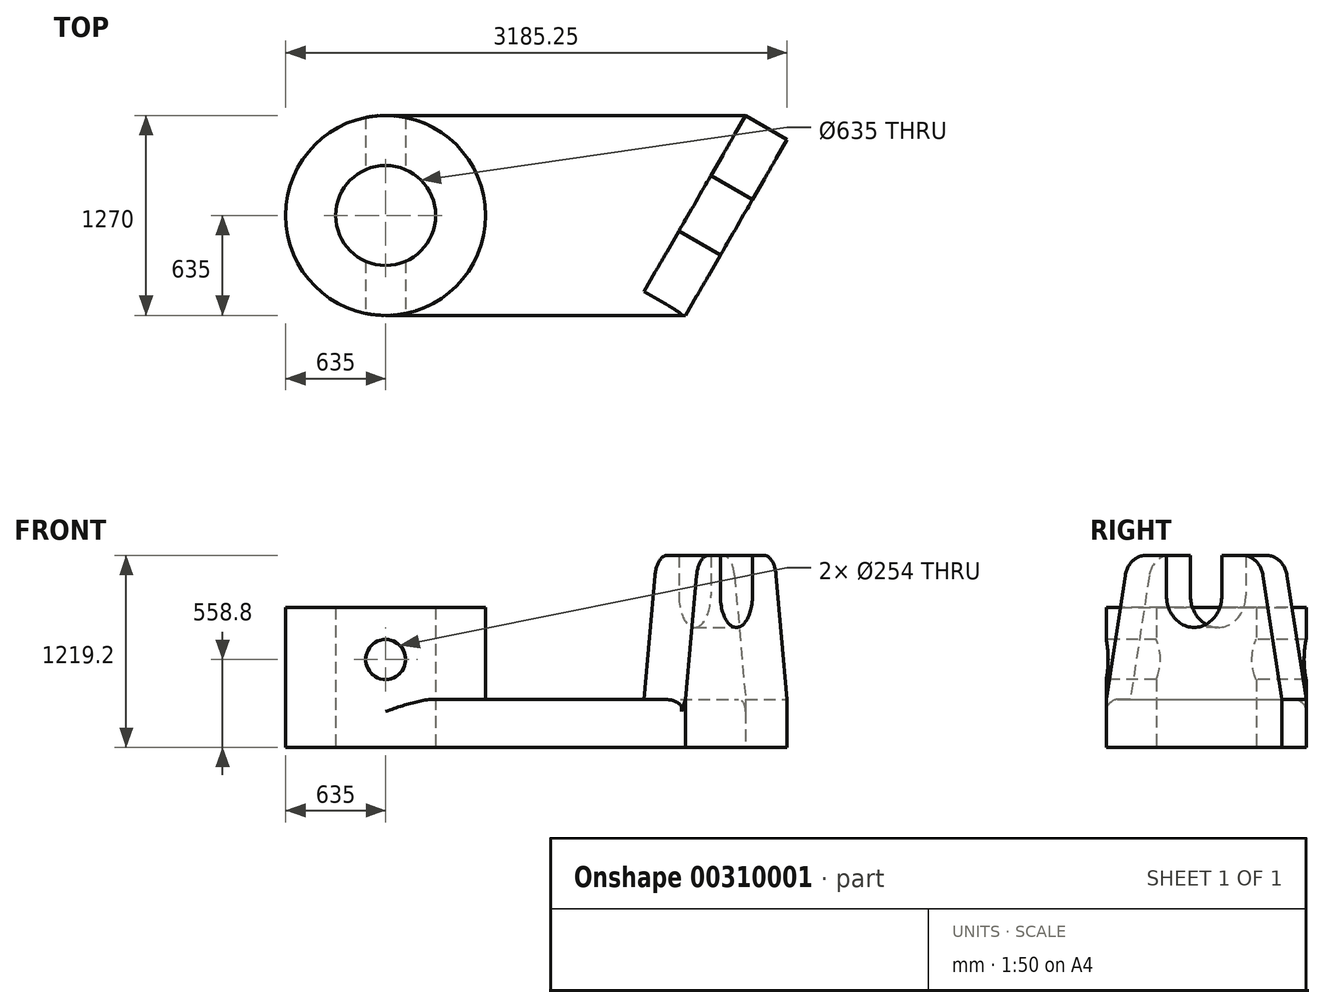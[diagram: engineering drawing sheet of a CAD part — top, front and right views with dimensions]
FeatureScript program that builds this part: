
annotation { "Feature Type Name" : "Feature", "Feature Type Description" : "" }
export const myFeature = defineFeature(function(context is Context, id is Id, definition is map)
    precondition{}
    {
        {
            var Q0;
            Q0=qCreatedBy(makeId("Top.planeOp"),FACE);
            var sketch = newSketch(context, id + "F0", { "sketchPlane" : qUnion([Q0])});
            skCircle(sketch, "E0", {"center": v(0, 0) * mm, "radius": 635 * mm});
            skCircle(sketch, "E1", {"center": v(0, 0) * mm, "radius": 317.5 * mm});
            skLineSegment(sketch, "E2.top", {"start": v(0, -635) * mm, "end": v(1905, -635) * mm});
            skLineSegment(sketch, "E3", {"start": v(1905, -635) * mm, "end": v(1641.04, -482.6) * mm});
            skLineSegment(sketch, "E4", {"start": v(1641.04, -482.6) * mm, "end": v(2286.28, 635) * mm});
            skLineSegment(sketch, "E5", {"start": v(1905, -635) * mm, "end": v(2550.25, 482.6) * mm});
            skLineSegment(sketch, "E6", {"start": v(2286.28, 635) * mm, "end": v(2550.25, 482.6) * mm});
            skLineSegment(sketch, "E7", {"start": v(0, 635) * mm, "end": v(2286.28, 635) * mm});
            skSolve(sketch);
        }
        {
            var Q0;
            Q0=makeQuery(id+"F0.imprint","IMPRINT",FACE,{"disambiguationData":[TD([[makeQuery(id+"F0.imprint","IMPRINT",EDGE,{"derivedFrom":sQuery(id+"F0.wireOp",EDGE,"E1")}),-1.0]])]});
            extrude(context, id + "F1", {"entities" : qUnion([Q0]), "depth" : 889 * mm});
        }
        {
            var Q0;
            {var subQ0=sQuery(id+"F0.wireOp",EDGE,"E2.top");Q0=makeQuery(id+"F0.imprint","IMPRINT",FACE,{"disambiguationData":[TD([[makeQuery(id+"F0.imprint","IMPRINT",EDGE,{"derivedFrom":subQ0}),1.0]])]});}
            var Q1;
            Q1=makeQuery(id+"F0.imprint","IMPRINT",FACE,{"disambiguationData":[TD([[makeQuery(id+"F0.imprint","IMPRINT",EDGE,{"derivedFrom":sQuery(id+"F0.wireOp",EDGE,"E3")}),-1.0]])]});
            extrude(context, id + "F2", {"entities" : qUnion([Q0, Q1]), "operationType" : NewBodyOperationType.ADD, "depth" : 304.8 * mm});
        }
        {
            var Q0;
            Q0=makeQuery(id+"F2.opExtrude","SWEPT_FACE",FACE,{"disambiguationData":[OSD([sQuery(id+"F0.wireOp",EDGE,"E5")])]});
            var sketch = newSketch(context, id + "F3", { "sketchPlane" : qUnion([Q0])});
            skLineSegment(sketch, "E8", {"start": v(692.9, 1219.2) * mm, "end": v(844.62, 1219.2) * mm});
            skLineSegment(sketch, "E9", {"start": v(1251.02, 1219.2) * mm, "end": v(1402.74, 1219.2) * mm});
            skLineSegment(sketch, "E10", {"start": v(1552.78, 1093.49) * mm, "end": v(1693.07, 304.8) * mm});
            skLineSegment(sketch, "E11", {"start": v(542.86, 1093.49) * mm, "end": v(402.57, 304.8) * mm});
            skPoint(sketch, "E12.visualSharp", {"position": v(1530.42, 1219.2) * mm});
            skArc(sketch, "E12.filletArc", {"start": v(1552.78, 1093.49) * mm, "mid": v(1500.6, 1183.62) * mm, "end": v(1402.74, 1219.2) * mm});
            skPoint(sketch, "E13.visualSharp", {"position": v(565.22, 1219.2) * mm});
            skArc(sketch, "E13.filletArc", {"start": v(692.9, 1219.2) * mm, "mid": v(595.03, 1183.62) * mm, "end": v(542.86, 1093.49) * mm});
            skLineSegment(sketch, "E14", {"start": v(692.9, 1219.2) * mm, "end": v(542.86, 1219.2) * mm, "construction": true});
            skLineSegment(sketch, "E15", {"start": v(1402.74, 1219.2) * mm, "end": v(1552.78, 1219.2) * mm, "construction": true});
            skLineSegment(sketch, "E16", {"start": v(844.62, 1219.2) * mm, "end": v(844.62, 965.2) * mm});
            skLineSegment(sketch, "E17", {"start": v(1251.02, 1219.2) * mm, "end": v(1251.02, 965.2) * mm});
            skPoint(sketch, "E18.centerSnap0", {"position": v(1047.82, 304.8) * mm});
            skArc(sketch, "E19", {"start": v(844.62, 965.2) * mm, "mid": v(1047.82, 762) * mm, "end": v(1251.02, 965.2) * mm});
            skSolve(sketch);
        }
        {
            var Q0;
            Q0=makeQuery(id+"F3.imprint","IMPRINT",FACE,{"disambiguationData":[TD([[makeQuery(id+"F3.imprint","IMPRINT",EDGE,{"derivedFrom":sQuery(id+"F3.wireOp",EDGE,"E8")}),-1.0]])]});
            extrude(context, id + "F4", {"entities" : qUnion([Q0]), "operationType" : NewBodyOperationType.ADD, "oppositeDirection" : true, "depth" : 304.8 * mm});
        }
        {
            var Q0;
            Q0=makeQuery(id+"F2.opExtrude","SWEPT_FACE",FACE,{"disambiguationData":[OSD([sQuery(id+"F0.wireOp",EDGE,"E2.top")])]});
            var sketch = newSketch(context, id + "F5", { "sketchPlane" : qUnion([Q0])});
            skPoint(sketch, "E20", {"position": v(0, 558.8) * mm});
            skSolve(sketch);
        }
        {
            var Q0;
            Q0=sQuery(id+"F5.wireOp",VERTEX,"E20");
            var Q1;
            Q1=makeQuery(id+"F1.opExtrude","SWEPT_BODY",BODY,{"disambiguationData":[OSD([sQuery(id+"F0.wireOp",EDGE,"E0"),sQuery(id+"F0.wireOp",EDGE,"E1")])]});
            hole(context, id + "F6", {"style" : HoleStyle.SIMPLE, "endStyle" : HoleEndStyle.THROUGH, "holeDiameter" : 254 * mm, "tappedDepth" : 12.7 * mm, "tapClearance" : 3, "locations" : qUnion([Q0]), "scope" : qUnion([Q1])});
        }
        {
            var Q0;
            Q0=makeQuery(id+"F2.opExtrude","CAP_EDGE",EDGE,{"disambiguationData":[OSD([sQuery(id+"F0.wireOp",EDGE,"E2.top")])],"isStart":false});
            var Q1;
            Q1=makeQuery(id+"F2.opExtrude","CAP_EDGE",EDGE,{"disambiguationData":[OSD([sQuery(id+"F0.wireOp",EDGE,"E0")])],"isStart":false});
            var Q2;
            Q2=makeQuery(id+"F2.opExtrude","CAP_EDGE",EDGE,{"disambiguationData":[OSD([sQuery(id+"F0.wireOp",EDGE,"E7")])],"isStart":false});
            fillet(context, id + "F7", {"entities" : qUnion([Q0, Q1, Q2]), "radius" : 76.2 * mm, "tangentPropagation" : true, "allowEdgeOverflow" : false});
        }
    });
